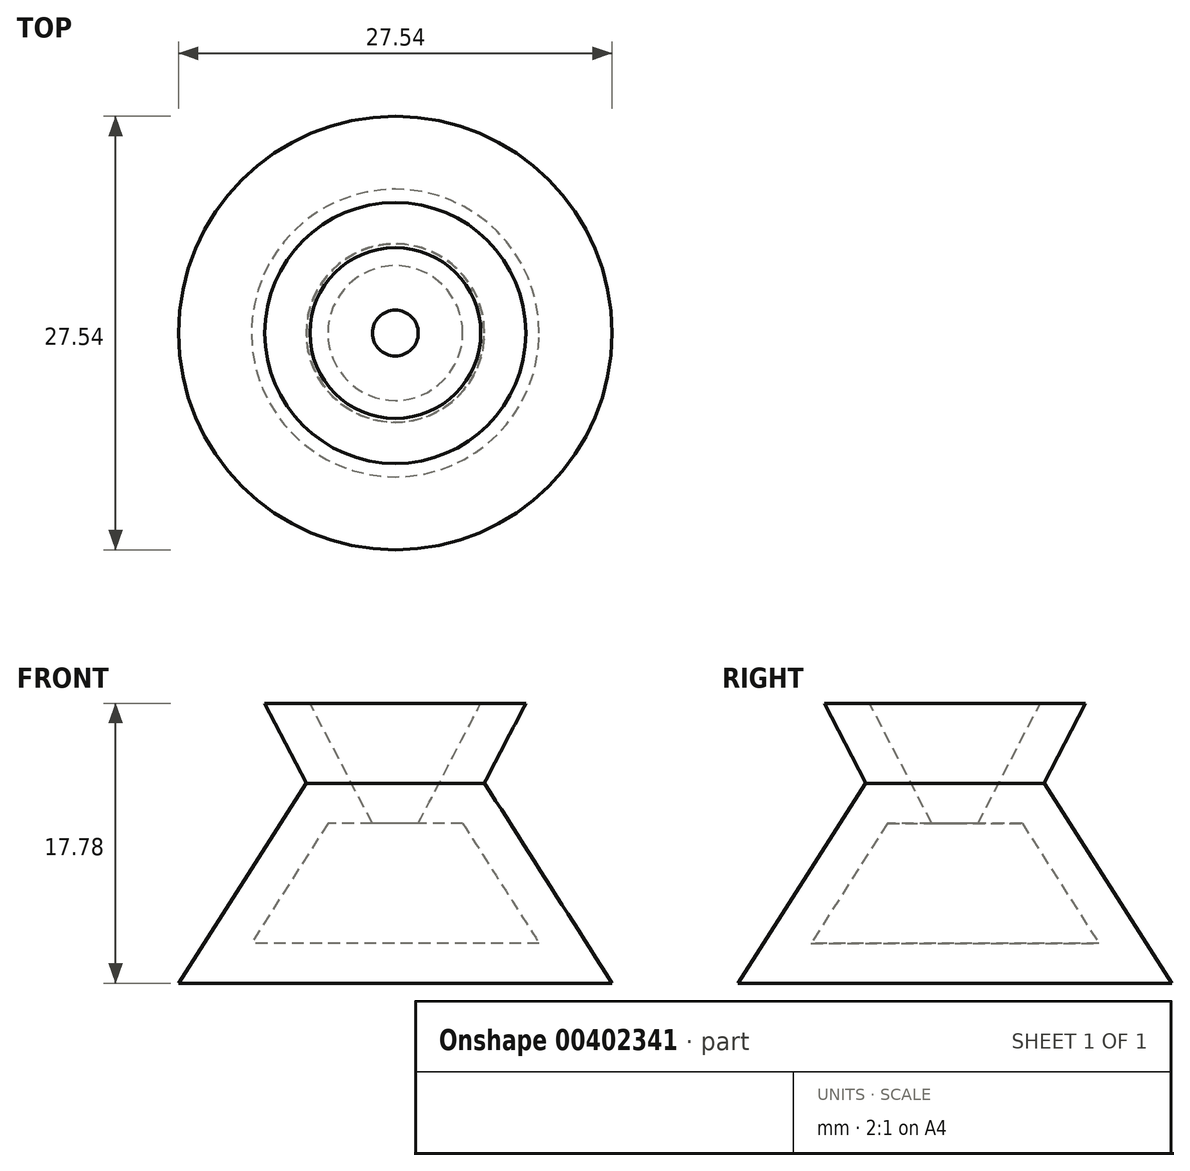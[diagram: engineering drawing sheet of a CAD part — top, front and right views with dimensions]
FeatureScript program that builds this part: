
annotation { "Feature Type Name" : "Feature", "Feature Type Description" : "" }
export const myFeature = defineFeature(function(context is Context, id is Id, definition is map)
    precondition{}
    {
        {
            var Q0;
            Q0=qCreatedBy(makeId("Top.planeOp"),FACE);
            cPlane(context, id + "F0", {"entities" : qUnion([Q0]), "cplaneType" : CPlaneType.OFFSET, "offset" : 12.7 * mm, "width" : 152.4 * mm, "height" : 152.4 * mm});
        }
        {
            var Q0;
            Q0=qCreatedBy(id+"F0.planeOp",FACE);
            var sketch = newSketch(context, id + "F1", { "sketchPlane" : qUnion([Q0])});
            skCircle(sketch, "E0", {"center": v(0, 0) * mm, "radius": 5.67 * mm});
            skSolve(sketch);
        }
        {
            var Q0;
            Q0=qCreatedBy(makeId("Top.planeOp"),FACE);
            var sketch = newSketch(context, id + "F2", { "sketchPlane" : qUnion([Q0])});
            skCircle(sketch, "E1", {"center": v(0, 0) * mm, "radius": 13.77 * mm});
            skSolve(sketch);
        }
        {
            var Q0;
            Q0=makeQuery(id+"F2.imprint","IMPRINT",FACE,{"disambiguationData":[TD([[makeQuery(id+"F2.imprint","IMPRINT",EDGE,{"derivedFrom":sQuery(id+"F2.wireOp",EDGE,"E1")}),1.0]])]});
            var Q1;
            Q1=makeQuery(id+"F1.imprint","IMPRINT",FACE,{"disambiguationData":[TD([[makeQuery(id+"F1.imprint","IMPRINT",EDGE,{"derivedFrom":sQuery(id+"F1.wireOp",EDGE,"E0")}),1.0]])]});
            loft(context, id + "F3", {"sheetProfilesArray" : [{ "sheetProfileEntities" : qUnion([Q0]) }, { "sheetProfileEntities" : qUnion([Q1]) }]});
        }
        {
            var Q0;
            Q0=qCreatedBy(id+"F0.planeOp",FACE);
            cPlane(context, id + "F4", {"entities" : qUnion([Q0]), "cplaneType" : CPlaneType.OFFSET, "offset" : 5.08 * mm, "width" : 152.4 * mm, "height" : 152.4 * mm});
        }
        {
            var Q0;
            Q0=qCreatedBy(id+"F0.planeOp",FACE);
            var sketch = newSketch(context, id + "F5", { "sketchPlane" : qUnion([Q0])});
            skCircle(sketch, "E2", {"center": v(0, 0) * mm, "radius": 5.64 * mm});
            skSolve(sketch);
        }
        {
            var Q0;
            Q0=qCreatedBy(id+"F4.planeOp",FACE);
            var sketch = newSketch(context, id + "F6", { "sketchPlane" : qUnion([Q0])});
            skCircle(sketch, "E3", {"center": v(0, 0) * mm, "radius": 8.29 * mm});
            skSolve(sketch);
        }
        {
            var Q1;
            Q1=makeQuery(id+"F6.imprint","IMPRINT",FACE,{"disambiguationData":[TD([[makeQuery(id+"F6.imprint","IMPRINT",EDGE,{"derivedFrom":sQuery(id+"F6.wireOp",EDGE,"E3")}),1.0]])]});
            var Q2;
            Q2=makeQuery(id+"F5.imprint","IMPRINT",FACE,{"disambiguationData":[TD([[makeQuery(id+"F5.imprint","IMPRINT",EDGE,{"derivedFrom":sQuery(id+"F5.wireOp",EDGE,"E2")}),1.0]])]});
            loft(context, id + "F7", {"operationType" : NewBodyOperationType.ADD, "sheetProfilesArray" : [{ "sheetProfileEntities" : qUnion([Q1]) }, { "sheetProfileEntities" : qUnion([Q2]) }]});
        }
        {
            var Q0;
            Q0=makeQuery(id+"F7.opLoft","CAP_FACE",FACE,{"disambiguationData":[OSD([makeQuery(id+"F6.imprint","IMPRINT",FACE,{"disambiguationData":[TD([[makeQuery(id+"F6.imprint","IMPRINT",EDGE,{"derivedFrom":sQuery(id+"F6.wireOp",EDGE,"E3")}),1.0]])]})])],"isStart":true});
            shell(context, id + "F8", {"entities" : qUnion([Q0]), "thickness" : 2.54 * mm});
        }
    });
